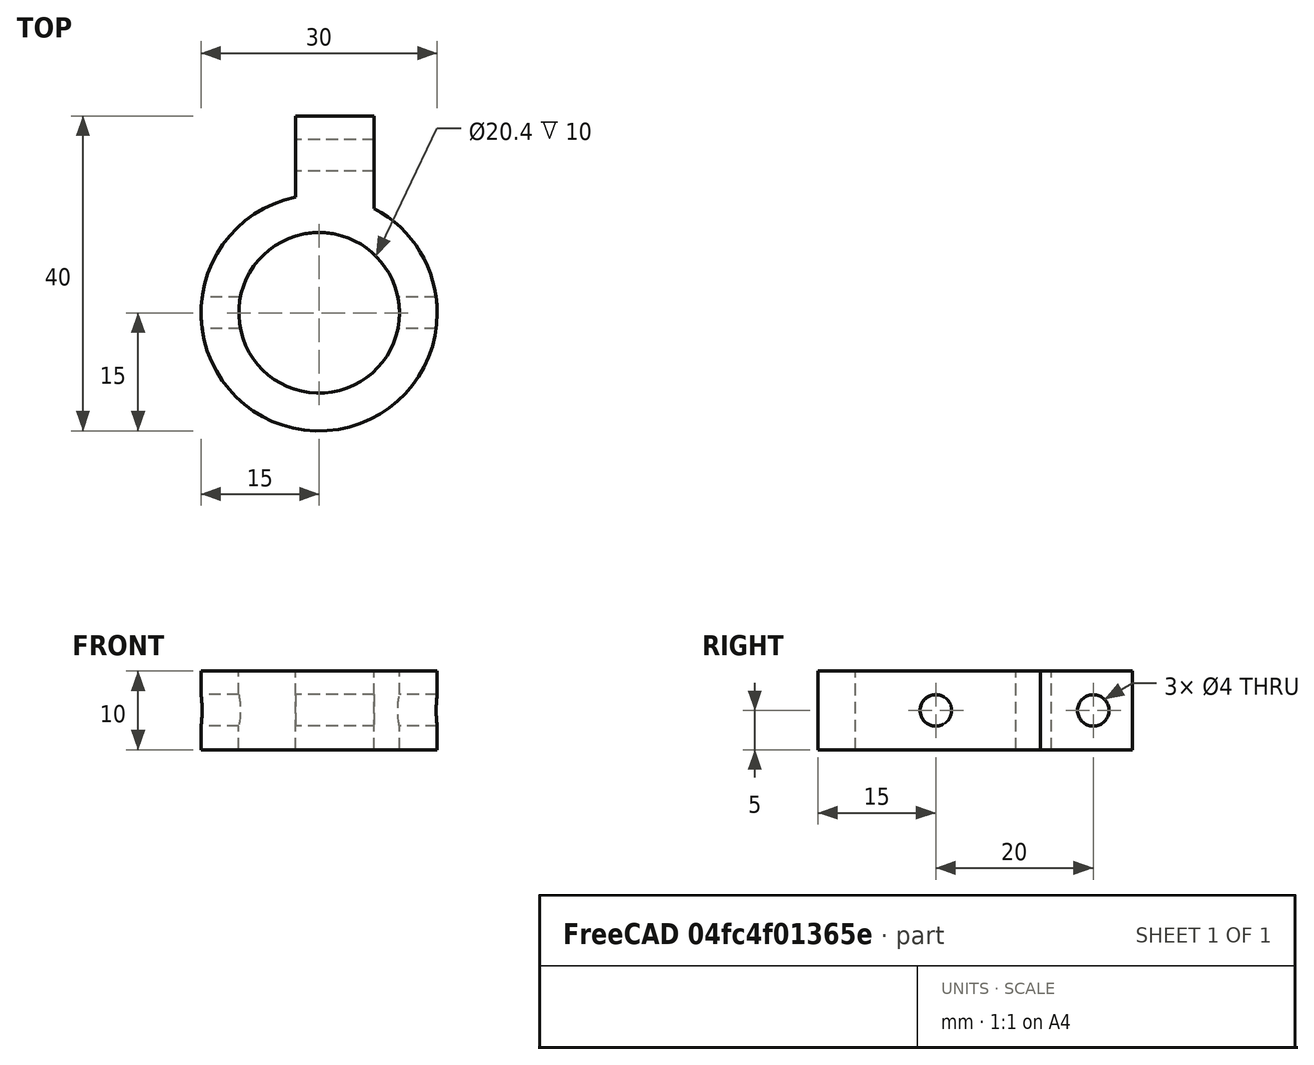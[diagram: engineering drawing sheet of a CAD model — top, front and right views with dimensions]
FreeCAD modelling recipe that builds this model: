
FCSTD DOCUMENT  (FreeCAD 0.18R16110 (Git))
Label: BaseAttachment2
License: All rights reserved
LicenseURL: http://en.wikipedia.org/wiki/All_rights_reserved
objects: Part::Cylinder×4, Part::MultiFuse×2, Part::Box×1, Part::Cut×1
note: 8 computed .brp shape members not serialized (recipe doc carries the construction recipe); baked Part::Feature solids carry a one-line shape summary decoded from their .brp

FEATURE [Part::Cylinder] Cylinder
  Angle = 360
  AttacherType = Attacher::AttachEngine3D
  Height = 10
  Placement = pos=(0,0,-5) rot=(0,0,1;0rad)
  Radius = 15
FEATURE [Part::Cylinder] Cylinder001
  Angle = 360
  AttacherType = Attacher::AttachEngine3D
  Height = 10
  Placement = pos=(0,0,-5) rot=(0,0,1;0rad)
  Radius = 10.2
FEATURE [Part::Box] Box  label="Cube"
  AttacherType = Attacher::AttachEngine3D
  Height = 10
  Length = 10
  Placement = pos=(-3,10,-5) rot=(0,0,1;0rad)
  Width = 15
FEATURE [Part::Cylinder] Cylinder003
  Angle = 360
  AttacherType = Attacher::AttachEngine3D
  Height = 10
  Placement = pos=(7,20,1.7e-15) rot=(0,-1,0;1.5708rad)
  Radius = 2
FEATURE [Part::MultiFuse] Fusion001  label="Positive Fusion"
  Shapes = -> [Cylinder,Box]
FEATURE [Part::Cylinder] Cylinder004
  Angle = 360
  AttacherType = Attacher::AttachEngine3D
  Height = 30
  Placement = pos=(15,0,0) rot=(0,-1,0;1.5708rad)
  Radius = 2
FEATURE [Part::MultiFuse] Fusion  label="Negative Fusion"
  Shapes = -> [Cylinder001,Cylinder003,Cylinder004]
FEATURE [Part::Cut] Cut
  Base = -> Fusion001
  Tool = -> Fusion
